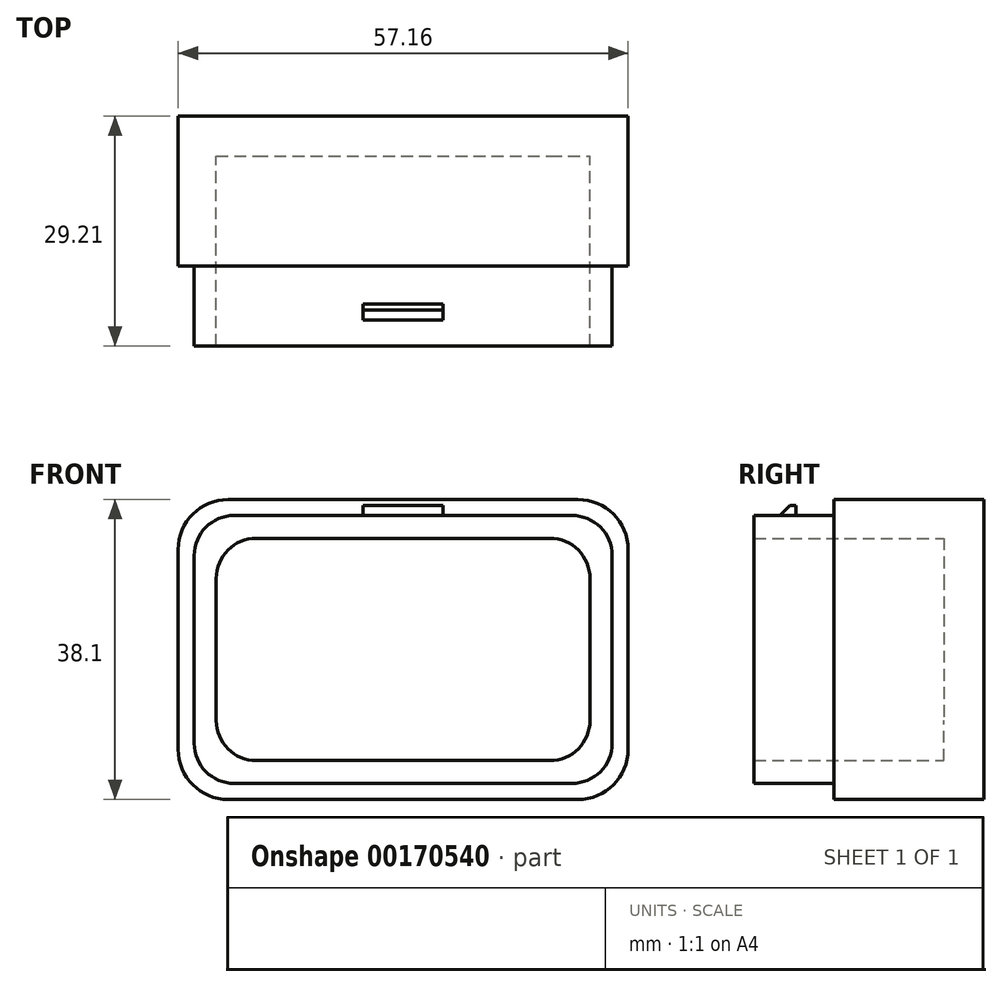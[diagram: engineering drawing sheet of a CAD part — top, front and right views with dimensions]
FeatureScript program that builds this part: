
annotation { "Feature Type Name" : "Feature", "Feature Type Description" : "" }
export const myFeature = defineFeature(function(context is Context, id is Id, definition is map)
    precondition{}
    {
        {
            var Q0;
            Q0=qCreatedBy(makeId("Front.planeOp"),FACE);
            var sketch = newSketch(context, id + "F0", { "sketchPlane" : qUnion([Q0])});
            skLineSegment(sketch, "E0.bottom", {"start": v(22.23, 19.05) * mm, "end": v(-22.23, 19.05) * mm});
            skLineSegment(sketch, "E0.top", {"start": v(22.23, -19.05) * mm, "end": v(-22.23, -19.05) * mm});
            skLineSegment(sketch, "E0.left", {"start": v(28.58, 12.7) * mm, "end": v(28.58, -12.7) * mm});
            skLineSegment(sketch, "E0.right", {"start": v(-28.58, 12.7) * mm, "end": v(-28.58, -12.7) * mm});
            skPoint(sketch, "E0.middle", {"position": v(0, 0) * mm});
            skLineSegment(sketch, "E1.bottom", {"start": v(21.46, 17.02) * mm, "end": v(-21.46, 17.02) * mm});
            skLineSegment(sketch, "E1.top", {"start": v(21.46, -17.02) * mm, "end": v(-21.46, -17.02) * mm});
            skLineSegment(sketch, "E1.left", {"start": v(26.54, 11.94) * mm, "end": v(26.54, -11.94) * mm});
            skLineSegment(sketch, "E1.right", {"start": v(-26.54, 11.94) * mm, "end": v(-26.54, -11.94) * mm});
            skPoint(sketch, "E2.visualSharp", {"position": v(28.58, 19.05) * mm});
            skArc(sketch, "E2.filletArc", {"start": v(28.58, 12.7) * mm, "mid": v(26.72, 17.2) * mm, "end": v(22.23, 19.05) * mm});
            skPoint(sketch, "E3.visualSharp", {"position": v(28.58, -19.05) * mm});
            skArc(sketch, "E3.filletArc", {"start": v(22.23, -19.05) * mm, "mid": v(26.72, -17.2) * mm, "end": v(28.58, -12.7) * mm});
            skPoint(sketch, "E4.visualSharp", {"position": v(-28.58, -19.05) * mm});
            skArc(sketch, "E4.filletArc", {"start": v(-28.58, -12.7) * mm, "mid": v(-26.72, -17.2) * mm, "end": v(-22.23, -19.05) * mm});
            skPoint(sketch, "E5.visualSharp", {"position": v(-28.58, 19.05) * mm});
            skArc(sketch, "E5.filletArc", {"start": v(-22.23, 19.05) * mm, "mid": v(-26.72, 17.2) * mm, "end": v(-28.58, 12.7) * mm});
            skPoint(sketch, "E6.visualSharp", {"position": v(-26.54, 17.02) * mm});
            skArc(sketch, "E6.filletArc", {"start": v(-21.46, 17.02) * mm, "mid": v(-25.06, 15.53) * mm, "end": v(-26.54, 11.94) * mm});
            skPoint(sketch, "E7.visualSharp", {"position": v(-26.54, -17.02) * mm});
            skArc(sketch, "E7.filletArc", {"start": v(-26.54, -11.94) * mm, "mid": v(-25.06, -15.53) * mm, "end": v(-21.46, -17.02) * mm});
            skPoint(sketch, "E8.visualSharp", {"position": v(26.54, -17.02) * mm});
            skArc(sketch, "E8.filletArc", {"start": v(21.46, -17.02) * mm, "mid": v(25.06, -15.53) * mm, "end": v(26.54, -11.94) * mm});
            skPoint(sketch, "E9.visualSharp", {"position": v(26.54, 17.02) * mm});
            skArc(sketch, "E9.filletArc", {"start": v(26.54, 11.94) * mm, "mid": v(25.06, 15.53) * mm, "end": v(21.46, 17.02) * mm});
            skLineSegment(sketch, "E10.bottom", {"start": v(-18.66, 14.12) * mm, "end": v(18.66, 14.12) * mm});
            skLineSegment(sketch, "E10.top", {"start": v(-18.66, -14.12) * mm, "end": v(18.66, -14.12) * mm});
            skLineSegment(sketch, "E10.left", {"start": v(-23.74, 9.04) * mm, "end": v(-23.74, -9.04) * mm});
            skLineSegment(sketch, "E10.right", {"start": v(23.74, 9.04) * mm, "end": v(23.74, -9.04) * mm});
            skPoint(sketch, "E11.visualSharp", {"position": v(23.74, 14.12) * mm});
            skArc(sketch, "E11.filletArc", {"start": v(23.74, 9.04) * mm, "mid": v(22.25, 12.63) * mm, "end": v(18.66, 14.12) * mm});
            skPoint(sketch, "E12.visualSharp", {"position": v(23.74, -14.12) * mm});
            skArc(sketch, "E12.filletArc", {"start": v(18.66, -14.12) * mm, "mid": v(22.25, -12.63) * mm, "end": v(23.74, -9.04) * mm});
            skPoint(sketch, "E13.visualSharp", {"position": v(-23.74, -14.12) * mm});
            skArc(sketch, "E13.filletArc", {"start": v(-23.74, -9.04) * mm, "mid": v(-22.25, -12.63) * mm, "end": v(-18.66, -14.12) * mm});
            skPoint(sketch, "E14.visualSharp", {"position": v(-23.74, 14.12) * mm});
            skArc(sketch, "E14.filletArc", {"start": v(-18.66, 14.12) * mm, "mid": v(-22.25, 12.63) * mm, "end": v(-23.74, 9.04) * mm});
            skSolve(sketch);
        }
        {
            var Q0;
            Q0=makeQuery(id+"F0.imprint","IMPRINT",FACE,{"disambiguationData":[TD([[makeQuery(id+"F0.imprint","IMPRINT",EDGE,{"derivedFrom":sQuery(id+"F0.wireOp",EDGE,"E0.bottom")}),1.0]])]});
            extrude(context, id + "F1", {"entities" : qUnion([Q0]), "depth" : 19.05 * mm});
        }
        {
            var Q0;
            Q0=makeQuery(id+"F0.imprint","IMPRINT",FACE,{"disambiguationData":[TD([[makeQuery(id+"F0.imprint","IMPRINT",EDGE,{"derivedFrom":sQuery(id+"F0.wireOp",EDGE,"E1.bottom")}),1.0]])]});
            extrude(context, id + "F2", {"entities" : qUnion([Q0]), "operationType" : NewBodyOperationType.ADD, "depth" : 29.2 * mm});
        }
        {
            var Q0;
            Q0=makeQuery(id+"F0.imprint","IMPRINT",FACE,{"disambiguationData":[TD([[makeQuery(id+"F0.imprint","IMPRINT",EDGE,{"derivedFrom":sQuery(id+"F0.wireOp",EDGE,"E10.bottom")}),-1.0]])]});
            extrude(context, id + "F3", {"entities" : qUnion([Q0]), "operationType" : NewBodyOperationType.ADD, "depth" : 5.08 * mm});
        }
        {
            var Q0;
            Q0=makeQuery(id+"F2.opExtrude","SWEPT_FACE",FACE,{"disambiguationData":[OSD([sQuery(id+"F0.wireOp",EDGE,"E1.bottom")])]});
            var sketch = newSketch(context, id + "F4", { "sketchPlane" : qUnion([Q0])});
            skLineSegment(sketch, "E15.bottom", {"start": v(-5.08, -23.9) * mm, "end": v(5.08, -23.9) * mm});
            skLineSegment(sketch, "E15.top", {"start": v(-5.08, -25.93) * mm, "end": v(5.08, -25.93) * mm});
            skLineSegment(sketch, "E15.left", {"start": v(-5.08, -23.9) * mm, "end": v(-5.08, -25.93) * mm});
            skLineSegment(sketch, "E15.right", {"start": v(5.08, -23.9) * mm, "end": v(5.08, -25.93) * mm});
            skPoint(sketch, "E15.middle", {"position": v(0, -24.92) * mm});
            skSolve(sketch);
        }
        {
            var Q0;
            Q0=makeQuery(id+"F4.imprint","IMPRINT",FACE,{"disambiguationData":[TD([[makeQuery(id+"F4.imprint","IMPRINT",EDGE,{"derivedFrom":sQuery(id+"F4.wireOp",EDGE,"E15.bottom")}),-1.0]])]});
            extrude(context, id + "F5", {"entities" : qUnion([Q0]), "operationType" : NewBodyOperationType.ADD, "depth" : 1.27 * mm});
        }
        {
            var Q0;
            Q0=makeQuery(id+"F5.opExtrude","CAP_EDGE",EDGE,{"disambiguationData":[OSD([sQuery(id+"F4.wireOp",EDGE,"E15.top")])],"isStart":false});
            chamfer(context, id + "F6", {"entities" : qUnion([Q0]), "width" : 1.27 * mm, "tangentPropagation" : true});
        }
    });
